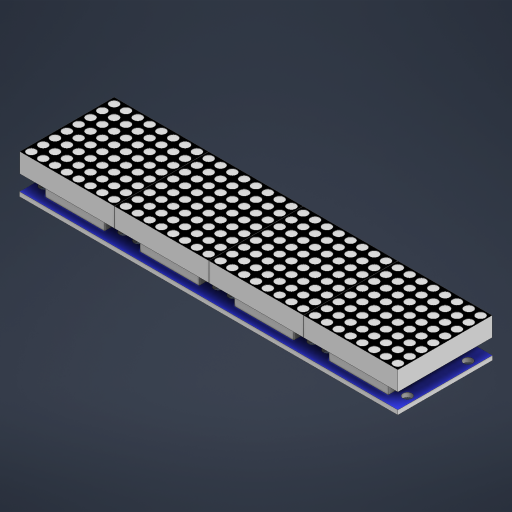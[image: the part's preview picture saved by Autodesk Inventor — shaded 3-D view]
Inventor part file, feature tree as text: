
AUTODESK INVENTOR PART (.ipt)
format: ipt  version: 2024 (Build 280153000, 153)  size: 771,072 bytes
history: native  units: mm
features: extrude x4, sketch x4, projected_geometry x4, other x1
ambient origin geometry x8: Origin, YZ Plane, XZ Plane, XY Plane, X Axis, Y Axis, Z Axis, Center Point
bodies: Body1 (feature_tree)
feature tree (13):
  other  "솔리드1"
  extrude  "돌출1"  Depth=128.0mm
  extrude  "돌출2"  Depth=32.0mm
  extrude  "돌출3"  Depth=32.0mm
  extrude  "돌출4"  Depth=32.0mm
  sketch  "스케치1"
  sketch  "스케치2"
  projected_geometry  "투영된 루프1"
  projected_geometry  "투영된 루프2"
  sketch  "스케치3"
  projected_geometry  "투영된 루프3"
  sketch  "스케치4"
  projected_geometry  "투영된 루프4"
